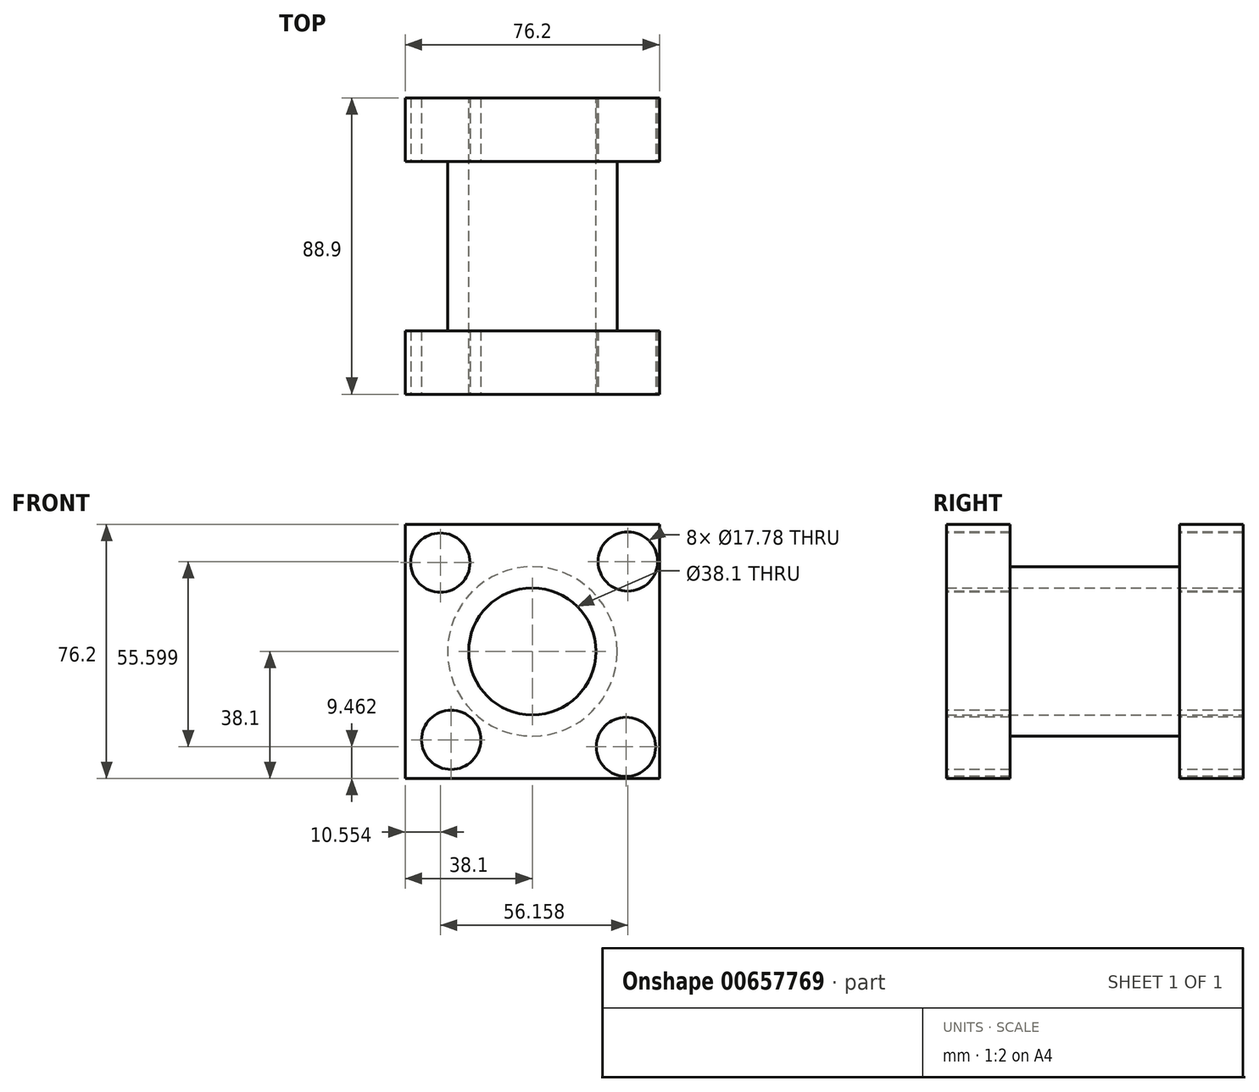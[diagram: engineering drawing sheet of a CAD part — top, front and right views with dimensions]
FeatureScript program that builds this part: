
annotation { "Feature Type Name" : "Feature", "Feature Type Description" : "" }
export const myFeature = defineFeature(function(context is Context, id is Id, definition is map)
    precondition{}
    {
        {
            var Q0;
            Q0=qCreatedBy(makeId("Front.planeOp"),FACE);
            var sketch = newSketch(context, id + "F0", { "sketchPlane" : qUnion([Q0])});
            skLineSegment(sketch, "E0.bottom", {"start": v(38.1, -38.1) * mm, "end": v(-38.1, -38.1) * mm});
            skLineSegment(sketch, "E0.top", {"start": v(38.1, 38.1) * mm, "end": v(-38.1, 38.1) * mm});
            skLineSegment(sketch, "E0.left", {"start": v(38.1, -38.1) * mm, "end": v(38.1, 38.1) * mm});
            skLineSegment(sketch, "E0.right", {"start": v(-38.1, -38.1) * mm, "end": v(-38.1, 38.1) * mm});
            skPoint(sketch, "E0.middle", {"position": v(0, 0) * mm});
            skSolve(sketch);
        }
        {
            var Q0;
            Q0=makeQuery(id+"F0.imprint","IMPRINT",FACE,{"disambiguationData":[TD([[makeQuery(id+"F0.imprint","IMPRINT",EDGE,{"derivedFrom":sQuery(id+"F0.wireOp",EDGE,"E0.bottom")}),-1.0]])]});
            extrude(context, id + "F1", {"entities" : qUnion([Q0]), "depth" : 19.05 * mm, "offsetDistance" : 25.4 * mm});
        }
        {
            var Q0;
            Q0=makeQuery(id+"F1.opExtrude","CAP_FACE",FACE,{"disambiguationData":[OSD([sQuery(id+"F0.wireOp",EDGE,"E0.bottom"),sQuery(id+"F0.wireOp",EDGE,"E0.top"),sQuery(id+"F0.wireOp",EDGE,"E0.left"),sQuery(id+"F0.wireOp",EDGE,"E0.right")])],"isStart":false});
            var sketch = newSketch(context, id + "F2", { "sketchPlane" : qUnion([Q0])});
            skCircle(sketch, "E1", {"center": v(0, 0) * mm, "radius": 25.4 * mm});
            skSolve(sketch);
        }
        {
            var Q0;
            Q0=makeQuery(id+"F2.imprint","IMPRINT",FACE,{"disambiguationData":[TD([[makeQuery(id+"F2.imprint","IMPRINT",EDGE,{"derivedFrom":sQuery(id+"F2.wireOp",EDGE,"E1")}),1.0]])]});
            var Q1;
            Q1=sQuery(id+"F2.wireOp",EDGE,"E1");
            extrude(context, id + "F3", {"entities" : qUnion([Q0]), "surfaceEntities" : qUnion([Q1]), "depth" : 25.4 * mm, "offsetDistance" : 25.4 * mm});
        }
        {
            var Q0;
            Q0=makeQuery(id+"F1.opExtrude","CAP_FACE",FACE,{"disambiguationData":[OSD([sQuery(id+"F0.wireOp",EDGE,"E0.bottom"),sQuery(id+"F0.wireOp",EDGE,"E0.top"),sQuery(id+"F0.wireOp",EDGE,"E0.left"),sQuery(id+"F0.wireOp",EDGE,"E0.right")])],"isStart":true});
            var sketch = newSketch(context, id + "F4", { "sketchPlane" : qUnion([Q0])});
            skCircle(sketch, "E2", {"center": v(0, 0) * mm, "radius": 25.4 * mm});
            skSolve(sketch);
        }
        {
            var Q0;
            Q0=makeQuery(id+"F1.opExtrude","SWEPT_BODY",BODY,{"disambiguationData":[OSD([sQuery(id+"F0.wireOp",EDGE,"E0.bottom"),sQuery(id+"F0.wireOp",EDGE,"E0.top"),sQuery(id+"F0.wireOp",EDGE,"E0.left"),sQuery(id+"F0.wireOp",EDGE,"E0.right")])]});
            var Q1;
            Q1=makeQuery(id+"F3.opExtrude","SWEPT_BODY",BODY,{"disambiguationData":[OSD([sQuery(id+"F2.wireOp",EDGE,"E1")])]});
            var Q2;
            Q2=makeQuery(id+"F3.opExtrude","CAP_FACE",FACE,{"disambiguationData":[OSD([sQuery(id+"F2.wireOp",EDGE,"E1")])],"isStart":false});
            mirror(context, id + "F5", {"operationType" : NewBodyOperationType.ADD, "entities" : qUnion([Q0, Q1]), "mirrorPlane" : qUnion([Q2])});
        }
        {
            var Q0;
            Q0=sQuery(id+"F4.wireOp",VERTEX,"E2.center");
            var Q1;
            Q1=makeQuery(id+"F1.opExtrude","SWEPT_BODY",BODY,{"disambiguationData":[OSD([sQuery(id+"F0.wireOp",EDGE,"E0.bottom"),sQuery(id+"F0.wireOp",EDGE,"E0.top"),sQuery(id+"F0.wireOp",EDGE,"E0.left"),sQuery(id+"F0.wireOp",EDGE,"E0.right")])]});
            var Q2;
            Q2=makeQuery(id+"F3.opExtrude","SWEPT_BODY",BODY,{"disambiguationData":[OSD([sQuery(id+"F2.wireOp",EDGE,"E1")])]});
            hole(context, id + "F6", {"style" : HoleStyle.SIMPLE, "endStyle" : HoleEndStyle.THROUGH, "holeDiameter" : 38.1 * mm, "majorDiameter" : 6.35 * mm, "isTappedThrough" : true, "tappedDepth" : 12.7 * mm, "tapClearance" : 3, "locations" : qUnion([Q0]), "scope" : qUnion([Q1, Q2])});
        }
        {
            var Q0;
            Q0=makeQuery(id+"F5.opPattern","COPY",FACE,{"derivedFrom":makeQuery(id+"F1.opExtrude","CAP_FACE",FACE,{"disambiguationData":[OSD([sQuery(id+"F0.wireOp",EDGE,"E0.bottom"),sQuery(id+"F0.wireOp",EDGE,"E0.top"),sQuery(id+"F0.wireOp",EDGE,"E0.left"),sQuery(id+"F0.wireOp",EDGE,"E0.right")])],"isStart":true}),"instanceName":"1"});
            var sketch = newSketch(context, id + "F7", { "sketchPlane" : qUnion([Q0])});
            skCircle(sketch, "E3", {"center": v(28.08, -28.64) * mm, "radius": 6.84 * mm});
            skSolve(sketch);
        }
        {
            var Q0;
            Q0=sQuery(id+"F7.wireOp",VERTEX,"E3.center");
            var Q1;
            Q1=makeQuery(id+"F1.opExtrude","SWEPT_BODY",BODY,{"disambiguationData":[OSD([sQuery(id+"F0.wireOp",EDGE,"E0.bottom"),sQuery(id+"F0.wireOp",EDGE,"E0.top"),sQuery(id+"F0.wireOp",EDGE,"E0.left"),sQuery(id+"F0.wireOp",EDGE,"E0.right")])]});
            var Q2;
            Q2=makeQuery(id+"F3.opExtrude","SWEPT_BODY",BODY,{"disambiguationData":[OSD([sQuery(id+"F2.wireOp",EDGE,"E1")])]});
            hole(context, id + "F8", {"style" : HoleStyle.SIMPLE, "endStyle" : HoleEndStyle.THROUGH, "holeDiameter" : 17.78 * mm, "majorDiameter" : 6.35 * mm, "isTappedThrough" : true, "tappedDepth" : 12.7 * mm, "tapClearance" : 3, "locations" : qUnion([Q0]), "scope" : qUnion([Q1, Q2])});
        }
        {
            var Q0;
            Q0=makeQuery(id+"F5.opPattern","COPY",FACE,{"derivedFrom":makeQuery(id+"F1.opExtrude","CAP_FACE",FACE,{"disambiguationData":[OSD([sQuery(id+"F0.wireOp",EDGE,"E0.bottom"),sQuery(id+"F0.wireOp",EDGE,"E0.top"),sQuery(id+"F0.wireOp",EDGE,"E0.left"),sQuery(id+"F0.wireOp",EDGE,"E0.right")])],"isStart":true}),"instanceName":"1"});
            var sketch = newSketch(context, id + "F9", { "sketchPlane" : qUnion([Q0])});
            skCircle(sketch, "E4", {"center": v(-24.33, -26.51) * mm, "radius": 8.27 * mm});
            skSolve(sketch);
        }
        {
            var Q0;
            Q0=sQuery(id+"F9.wireOp",VERTEX,"E4.center");
            var Q1;
            Q1=makeQuery(id+"F1.opExtrude","SWEPT_BODY",BODY,{"disambiguationData":[OSD([sQuery(id+"F0.wireOp",EDGE,"E0.bottom"),sQuery(id+"F0.wireOp",EDGE,"E0.top"),sQuery(id+"F0.wireOp",EDGE,"E0.left"),sQuery(id+"F0.wireOp",EDGE,"E0.right")])]});
            var Q2;
            Q2=makeQuery(id+"F3.opExtrude","SWEPT_BODY",BODY,{"disambiguationData":[OSD([sQuery(id+"F2.wireOp",EDGE,"E1")])]});
            hole(context, id + "F10", {"style" : HoleStyle.SIMPLE, "endStyle" : HoleEndStyle.THROUGH, "holeDiameter" : 17.78 * mm, "majorDiameter" : 6.35 * mm, "isTappedThrough" : true, "tappedDepth" : 12.7 * mm, "tapClearance" : 3, "locations" : qUnion([Q0]), "scope" : qUnion([Q1, Q2])});
        }
        {
            var Q0;
            Q0=makeQuery(id+"F5.opPattern","COPY",FACE,{"derivedFrom":makeQuery(id+"F1.opExtrude","CAP_FACE",FACE,{"disambiguationData":[OSD([sQuery(id+"F0.wireOp",EDGE,"E0.bottom"),sQuery(id+"F0.wireOp",EDGE,"E0.top"),sQuery(id+"F0.wireOp",EDGE,"E0.left"),sQuery(id+"F0.wireOp",EDGE,"E0.right")])],"isStart":true}),"instanceName":"1"});
            var sketch = newSketch(context, id + "F11", { "sketchPlane" : qUnion([Q0])});
            skCircle(sketch, "E5", {"center": v(28.61, 26.96) * mm, "radius": 7.41 * mm});
            skCircle(sketch, "E6", {"center": v(-27.24, 27.87) * mm, "radius": 7.39 * mm});
            skSolve(sketch);
        }
        {
            var Q0;
            Q0=sQuery(id+"F11.wireOp",VERTEX,"E5.center");
            var Q1;
            Q1=makeQuery(id+"F1.opExtrude","SWEPT_BODY",BODY,{"disambiguationData":[OSD([sQuery(id+"F0.wireOp",EDGE,"E0.bottom"),sQuery(id+"F0.wireOp",EDGE,"E0.top"),sQuery(id+"F0.wireOp",EDGE,"E0.left"),sQuery(id+"F0.wireOp",EDGE,"E0.right")])]});
            var Q2;
            Q2=makeQuery(id+"F3.opExtrude","SWEPT_BODY",BODY,{"disambiguationData":[OSD([sQuery(id+"F2.wireOp",EDGE,"E1")])]});
            hole(context, id + "F12", {"style" : HoleStyle.SIMPLE, "endStyle" : HoleEndStyle.THROUGH, "holeDiameter" : 17.78 * mm, "majorDiameter" : 6.35 * mm, "isTappedThrough" : true, "tappedDepth" : 12.7 * mm, "tapClearance" : 3, "locations" : qUnion([Q0]), "scope" : qUnion([Q1, Q2])});
        }
        {
            var Q0;
            Q0=makeQuery(id+"F5.opPattern","COPY",FACE,{"derivedFrom":makeQuery(id+"F1.opExtrude","CAP_FACE",FACE,{"disambiguationData":[OSD([sQuery(id+"F0.wireOp",EDGE,"E0.bottom"),sQuery(id+"F0.wireOp",EDGE,"E0.top"),sQuery(id+"F0.wireOp",EDGE,"E0.left"),sQuery(id+"F0.wireOp",EDGE,"E0.right")])],"isStart":true}),"instanceName":"1"});
            var sketch = newSketch(context, id + "F13", { "sketchPlane" : qUnion([Q0])});
            skCircle(sketch, "E7", {"center": v(-27.55, 26.62) * mm, "radius": 7.64 * mm});
            skSolve(sketch);
        }
        {
            var Q0;
            Q0=sQuery(id+"F13.wireOp",VERTEX,"E7.center");
            var Q1;
            Q1=makeQuery(id+"F1.opExtrude","SWEPT_BODY",BODY,{"disambiguationData":[OSD([sQuery(id+"F0.wireOp",EDGE,"E0.bottom"),sQuery(id+"F0.wireOp",EDGE,"E0.top"),sQuery(id+"F0.wireOp",EDGE,"E0.left"),sQuery(id+"F0.wireOp",EDGE,"E0.right")])]});
            var Q2;
            Q2=makeQuery(id+"F3.opExtrude","SWEPT_BODY",BODY,{"disambiguationData":[OSD([sQuery(id+"F2.wireOp",EDGE,"E1")])]});
            hole(context, id + "F14", {"style" : HoleStyle.SIMPLE, "endStyle" : HoleEndStyle.THROUGH, "holeDiameter" : 17.78 * mm, "majorDiameter" : 6.35 * mm, "isTappedThrough" : true, "tappedDepth" : 12.7 * mm, "tapClearance" : 3, "locations" : qUnion([Q0]), "scope" : qUnion([Q1, Q2])});
        }
    });
